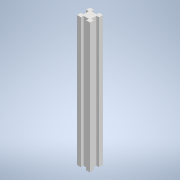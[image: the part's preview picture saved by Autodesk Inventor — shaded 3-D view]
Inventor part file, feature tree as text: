
AUTODESK INVENTOR PART (.ipt)
format: ipt  version: 2021 (Build 250183000, 183)  size: 117,760 bytes
history: native  units: mm
features: other x1, extrude x1, sketch x1
ambient origin geometry x8: Origin, YZ Plane, XZ Plane, XY Plane, X Axis, Y Axis, Z Axis, Center Point
bodies: Body1 (feature_tree)
feature tree (3):
  other  "Bryła1"
  extrude  "Wyciągnięcie proste1"  Depth=50.0mm
  sketch  "Szkic1"
